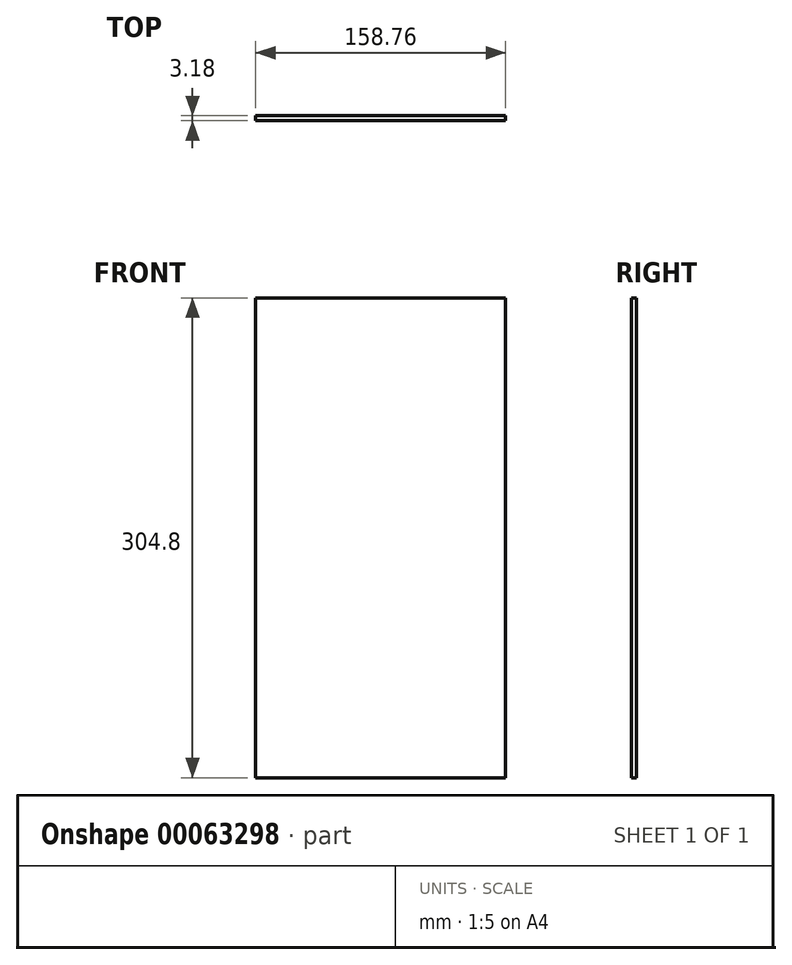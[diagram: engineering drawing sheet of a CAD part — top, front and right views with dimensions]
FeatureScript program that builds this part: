
annotation { "Feature Type Name" : "Feature", "Feature Type Description" : "" }
export const myFeature = defineFeature(function(context is Context, id is Id, definition is map)
    precondition{}
    {
        {
            var Q0;
            Q0=qCreatedBy(makeId("Front.planeOp"),FACE);
            var sketch = newSketch(context, id + "F0", { "sketchPlane" : qUnion([Q0])});
            skLineSegment(sketch, "E0.rect.bottom", {"start": v(79.38, 152.4) * mm, "end": v(-79.38, 152.4) * mm});
            skLineSegment(sketch, "E0.rect.top", {"start": v(79.38, -152.4) * mm, "end": v(-79.38, -152.4) * mm});
            skLineSegment(sketch, "E0.rect.left", {"start": v(79.38, 152.4) * mm, "end": v(79.37, -152.4) * mm});
            skLineSegment(sketch, "E0.rect.right", {"start": v(-79.38, 152.4) * mm, "end": v(-79.38, -152.4) * mm});
            skPoint(sketch, "E0.rect.middle", {"position": v(0, 0) * mm});
            skSolve(sketch);
        }
        {
            var Q0;
            Q0=makeQuery(id+"F0.imprint","IMPRINT",FACE,{"disambiguationData":[TD([[makeQuery(id+"F0.imprint","IMPRINT",EDGE,{"derivedFrom":sQuery(id+"F0.wireOp",EDGE,"E0.rect.bottom")}),1.0]])]});
            extrude(context, id + "F1", {"entities" : qUnion([Q0]), "depth" : 3.17 * mm, "symmetric" : true});
        }
    });
